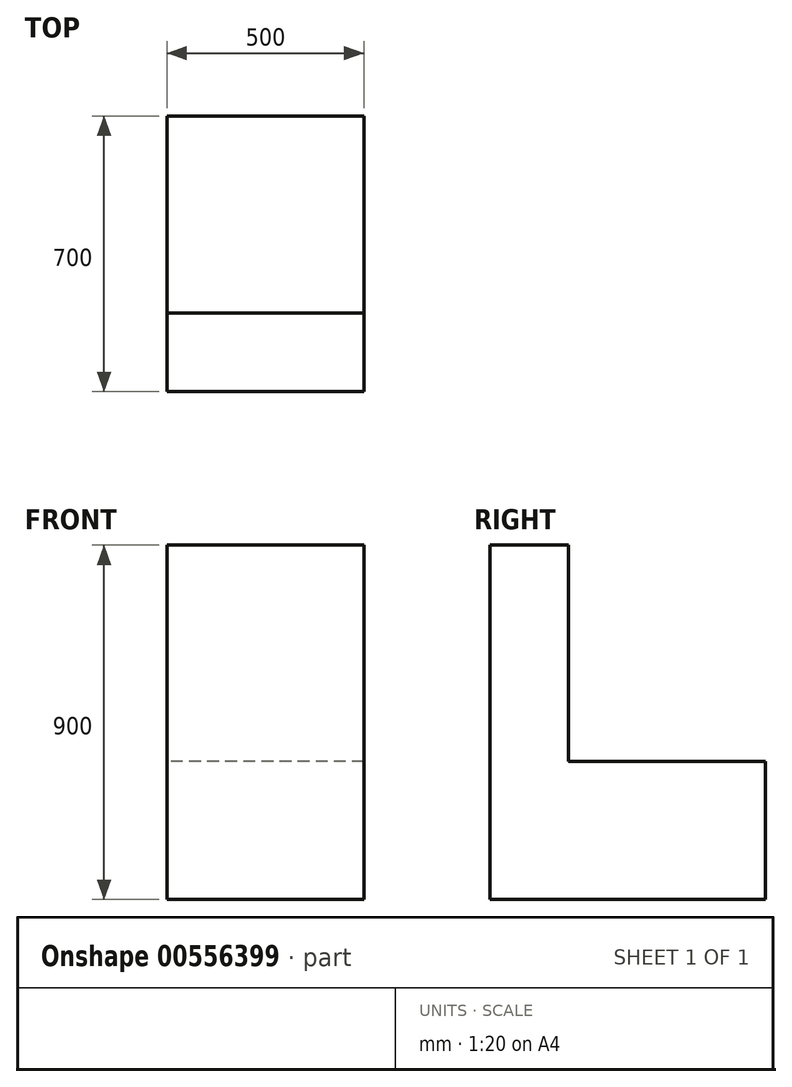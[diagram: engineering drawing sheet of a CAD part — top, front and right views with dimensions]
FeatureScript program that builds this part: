
annotation { "Feature Type Name" : "Feature", "Feature Type Description" : "" }
export const myFeature = defineFeature(function(context is Context, id is Id, definition is map)
    precondition{}
    {
        {
            var Q0;
            Q0=qCreatedBy(makeId("Right.planeOp"),FACE);
            var sketch = newSketch(context, id + "F0", { "sketchPlane" : qUnion([Q0])});
            skLineSegment(sketch, "E0.bottom", {"start": v(-250, -175) * mm, "end": v(250, -175) * mm});
            skLineSegment(sketch, "E0.top", {"start": v(-250, 175) * mm, "end": v(250, 175) * mm});
            skLineSegment(sketch, "E0.left", {"start": v(-250, -175) * mm, "end": v(-250, 175) * mm});
            skLineSegment(sketch, "E0.right", {"start": v(250, -175) * mm, "end": v(250, 175) * mm});
            skPoint(sketch, "E0.middle", {"position": v(0, 0) * mm});
            skLineSegment(sketch, "E1.bottom", {"start": v(-250, -175) * mm, "end": v(-450, -175) * mm});
            skLineSegment(sketch, "E1.top", {"start": v(-250, 725) * mm, "end": v(-450, 725) * mm});
            skLineSegment(sketch, "E1.left", {"start": v(-250, -175) * mm, "end": v(-250, 725) * mm});
            skLineSegment(sketch, "E1.right", {"start": v(-450, -175) * mm, "end": v(-450, 725) * mm});
            skSolve(sketch);
        }
        {
            var Q0;
            Q0=qSketchRegion(id+"F0",true);
            extrude(context, id + "F1", {"entities" : qUnion([Q0]), "depth" : 500 * mm});
        }
    });
